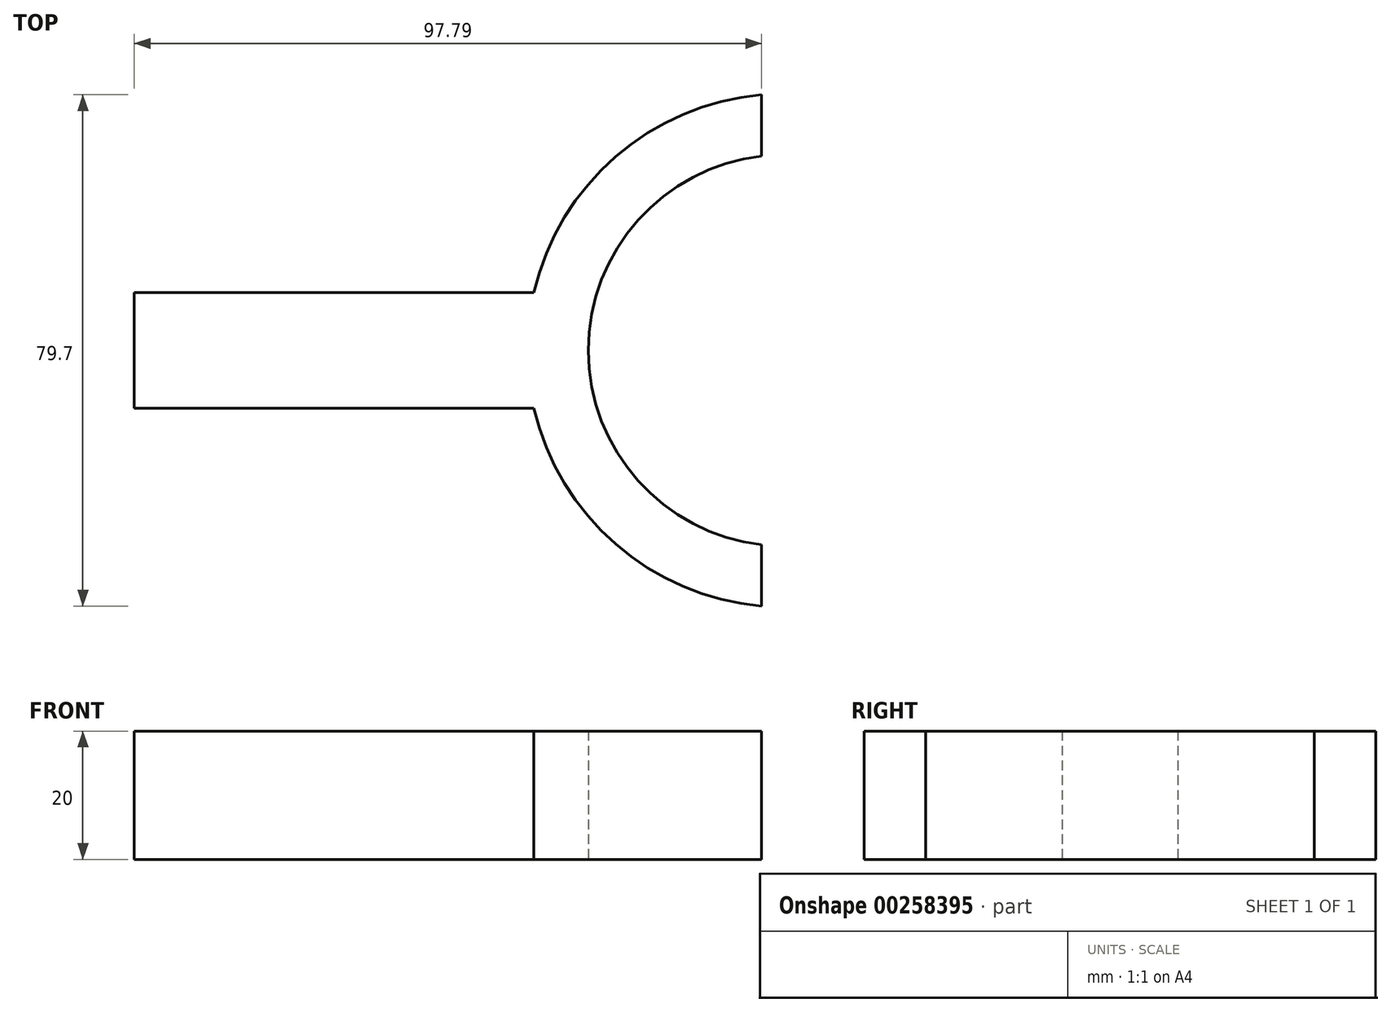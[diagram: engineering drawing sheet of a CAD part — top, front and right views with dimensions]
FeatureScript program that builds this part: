
annotation { "Feature Type Name" : "Feature", "Feature Type Description" : "" }
export const myFeature = defineFeature(function(context is Context, id is Id, definition is map)
    precondition{}
    {
        {
            var Q0;
            Q0=qCreatedBy(makeId("Top.planeOp"),FACE);
            var sketch = newSketch(context, id + "F0", { "sketchPlane" : qUnion([Q0])});
            skArc(sketch, "E0", {"start": v(-3.47, 30.3) * mm, "mid": v(-30.5, 0) * mm, "end": v(-3.47, -30.3) * mm});
            skArc(sketch, "E1", {"start": v(-3.47, 39.85) * mm, "mid": v(-40, 0) * mm, "end": v(-3.47, -39.85) * mm});
            skLineSegment(sketch, "E2.right", {"start": v(-101.26, -9) * mm, "end": v(-101.26, 9) * mm});
            skLineSegment(sketch, "E3", {"start": v(-3.47, 39.85) * mm, "end": v(-3.47, 30.3) * mm});
            skLineSegment(sketch, "E4.trimOffspring", {"start": v(-29.14, 9) * mm, "end": v(-101.26, 9) * mm});
            skLineSegment(sketch, "E5.trimOffspring", {"start": v(-29.14, -9) * mm, "end": v(-101.26, -9) * mm});
            skLineSegment(sketch, "E6.trimOffspring", {"start": v(-3.47, -30.3) * mm, "end": v(-3.47, -39.85) * mm});
            skPoint(sketch, "E7.MirrorCS.start.orphan", {"position": v(3.47, 39.85) * mm});
            skPoint(sketch, "E2.left.end.orphan", {"position": v(101.26, 9) * mm});
            skPoint(sketch, "E8.orphan", {"position": v(101.26, -9) * mm});
            skPoint(sketch, "E9.trimOffspring.end.orphan", {"position": v(3.47, -39.85) * mm});
            skSolve(sketch);
        }
        {
            var Q0;
            Q0=makeQuery(id+"F0.imprint","IMPRINT",FACE,{"disambiguationData":[TD([[makeQuery(id+"F0.imprint","IMPRINT",EDGE,{"derivedFrom":sQuery(id+"F0.wireOp",EDGE,"E0")}),-1.0]])]});
            var Q1;
            {var subQ5=sQuery(id+"F0.wireOp",EDGE,"E2.right");Q1=makeQuery(id+"F0.imprint","IMPRINT",FACE,{"disambiguationData":[TD([[makeQuery(id+"F0.imprint","IMPRINT",EDGE,{"derivedFrom":subQ5}),-1.0]])]});}
            var Q2;
            {var subQ5=sQuery(id+"F0.wireOp",EDGE,"E2.left");Q2=makeQuery(id+"F0.imprint","IMPRINT",FACE,{"disambiguationData":[TD([[makeQuery(id+"F0.imprint","IMPRINT",EDGE,{"derivedFrom":subQ5}),1.0]])]});}
            extrude(context, id + "F1", {"entities" : qUnion([Q0, Q1, Q2]), "depth" : 20 * mm});
        }
    });
